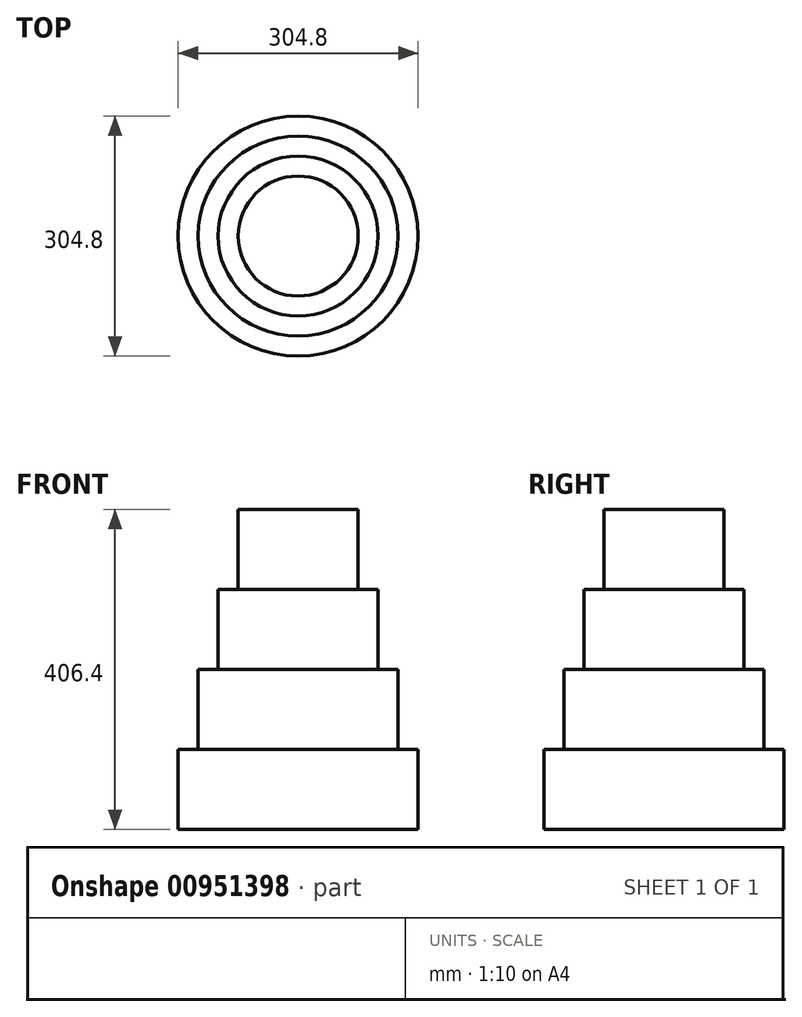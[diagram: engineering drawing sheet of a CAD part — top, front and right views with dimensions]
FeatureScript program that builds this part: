
annotation { "Feature Type Name" : "Feature", "Feature Type Description" : "" }
export const myFeature = defineFeature(function(context is Context, id is Id, definition is map)
    precondition{}
    {
        {
            var Q0;
            Q0=qCreatedBy(makeId("Front.planeOp"),FACE);
            var sketch = newSketch(context, id + "F0", { "sketchPlane" : qUnion([Q0])});
            skLineSegment(sketch, "E0.bottom", {"start": v(-152.4, 0) * mm, "end": v(152.4, 0) * mm});
            skLineSegment(sketch, "E0.top", {"start": v(-152.4, 127) * mm, "end": v(152.4, 127) * mm});
            skLineSegment(sketch, "E0.left", {"start": v(-152.4, 0) * mm, "end": v(-152.4, 127) * mm});
            skLineSegment(sketch, "E0.right", {"start": v(152.4, 0) * mm, "end": v(152.4, 127) * mm});
            skLineSegment(sketch, "E1.bottom", {"start": v(-127, 127) * mm, "end": v(127, 127) * mm});
            skLineSegment(sketch, "E1.top", {"start": v(-127, 254) * mm, "end": v(127, 254) * mm});
            skLineSegment(sketch, "E1.left", {"start": v(-127, 127) * mm, "end": v(-127, 254) * mm});
            skLineSegment(sketch, "E1.right", {"start": v(127, 127) * mm, "end": v(127, 254) * mm});
            skLineSegment(sketch, "E2.bottom", {"start": v(-101.6, 254) * mm, "end": v(101.6, 254) * mm});
            skLineSegment(sketch, "E2.top", {"start": v(-101.6, 381) * mm, "end": v(101.6, 381) * mm});
            skLineSegment(sketch, "E2.left", {"start": v(-101.6, 254) * mm, "end": v(-101.6, 381) * mm});
            skLineSegment(sketch, "E2.right", {"start": v(101.6, 254) * mm, "end": v(101.6, 381) * mm});
            skLineSegment(sketch, "E3.bottom", {"start": v(-76.2, 381) * mm, "end": v(76.2, 381) * mm});
            skLineSegment(sketch, "E3.top", {"start": v(-76.2, 508) * mm, "end": v(76.2, 508) * mm});
            skLineSegment(sketch, "E3.left", {"start": v(-76.2, 381) * mm, "end": v(-76.2, 508) * mm});
            skLineSegment(sketch, "E3.right", {"start": v(76.2, 381) * mm, "end": v(76.2, 508) * mm});
            skLineSegment(sketch, "E4", {"start": v(0, 508) * mm, "end": v(0, 0) * mm, "construction": true});
            skPoint(sketch, "E4.startSnap0", {"position": v(0, 508) * mm});
            skSolve(sketch);
        }
        {
            var Q0;
            Q0=qCreatedBy(makeId("Front.planeOp"),FACE);
            var sketch = newSketch(context, id + "F1", { "sketchPlane" : qUnion([Q0])});
            skLineSegment(sketch, "E5.bottom", {"start": v(425.8, 0) * mm, "end": v(578.2, 0) * mm});
            skLineSegment(sketch, "E5.left", {"start": v(273.4, 0) * mm, "end": v(273.4, 101.6) * mm, "construction": true});
            skLineSegment(sketch, "E5.right", {"start": v(578.2, 0) * mm, "end": v(578.2, 101.6) * mm});
            skLineSegment(sketch, "E6.bottom", {"start": v(425.8, 101.6) * mm, "end": v(552.8, 101.6) * mm});
            skLineSegment(sketch, "E6.left", {"start": v(298.8, 101.6) * mm, "end": v(298.8, 203.2) * mm, "construction": true});
            skLineSegment(sketch, "E6.right", {"start": v(552.8, 101.6) * mm, "end": v(552.8, 203.2) * mm});
            skLineSegment(sketch, "E7.bottom", {"start": v(425.8, 203.2) * mm, "end": v(527.4, 203.2) * mm});
            skLineSegment(sketch, "E7.left", {"start": v(324.2, 203.2) * mm, "end": v(324.2, 304.8) * mm, "construction": true});
            skLineSegment(sketch, "E7.right", {"start": v(527.4, 203.2) * mm, "end": v(527.4, 304.8) * mm});
            skLineSegment(sketch, "E8.bottom", {"start": v(425.8, 304.8) * mm, "end": v(502, 304.8) * mm});
            skLineSegment(sketch, "E8.top", {"start": v(425.8, 406.4) * mm, "end": v(502, 406.4) * mm});
            skLineSegment(sketch, "E8.left", {"start": v(349.6, 304.8) * mm, "end": v(349.6, 406.4) * mm, "construction": true});
            skLineSegment(sketch, "E8.right", {"start": v(502, 304.8) * mm, "end": v(502, 406.4) * mm});
            skLineSegment(sketch, "E9", {"start": v(425.8, 406.4) * mm, "end": v(425.8, -189.14) * mm});
            skPoint(sketch, "E9.startSnap0", {"position": v(425.8, 406.4) * mm});
            skLineSegment(sketch, "E10.trimOffspring", {"start": v(425.8, 203.2) * mm, "end": v(552.8, 203.2) * mm});
            skLineSegment(sketch, "E11.trimOffspring", {"start": v(425.8, 101.6) * mm, "end": v(578.2, 101.6) * mm});
            skLineSegment(sketch, "E12.trimOffspring", {"start": v(425.8, 304.8) * mm, "end": v(527.4, 304.8) * mm});
            skSolve(sketch);
        }
        {
            var Q0;
            Q0 = qSketchRegion(id + "F1", true);
            var Q1;
            Q1=sQuery(id+"F1.wireOp",EDGE,"E9");
            revolve(context, id + "F2", {"surfaceOperationType" : NewSurfaceOperationType.NEW, "entities" : qUnion([Q0]), "axis" : qUnion([Q1]), "revolveType" : RevolveType.FULL});
        }
    });
